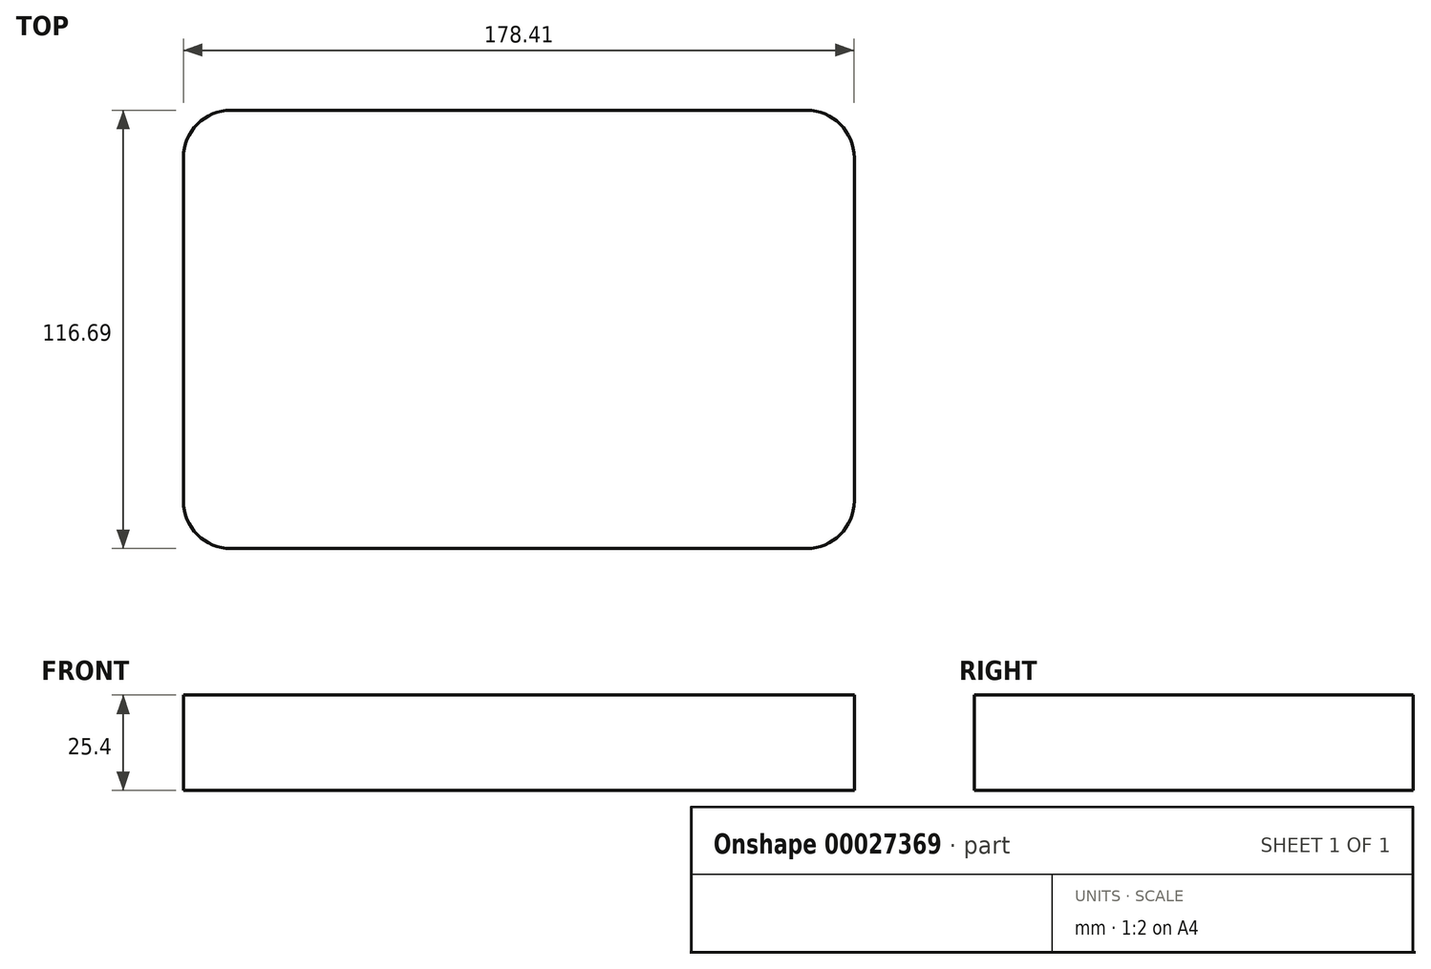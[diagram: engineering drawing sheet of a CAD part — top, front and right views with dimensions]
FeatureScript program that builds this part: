
annotation { "Feature Type Name" : "Feature", "Feature Type Description" : "" }
export const myFeature = defineFeature(function(context is Context, id is Id, definition is map)
    precondition{}
    {
        {
            var Q0;
            Q0=qCreatedBy(makeId("Top.planeOp"),FACE);
            var sketch = newSketch(context, id + "F0", { "sketchPlane" : qUnion([Q0])});
            skLineSegment(sketch, "E0.bottom", {"start": v(-115.93, 47.8) * mm, "end": v(37.08, 47.8) * mm});
            skLineSegment(sketch, "E0.top", {"start": v(-115.93, -68.9) * mm, "end": v(37.08, -68.9) * mm});
            skLineSegment(sketch, "E0.left", {"start": v(-128.63, 35.1) * mm, "end": v(-128.63, -56.2) * mm});
            skLineSegment(sketch, "E0.right", {"start": v(49.78, 35.1) * mm, "end": v(49.78, -56.2) * mm});
            skPoint(sketch, "E1.visualSharp", {"position": v(-128.63, 47.8) * mm});
            skArc(sketch, "E1.filletArc", {"start": v(-115.93, 47.8) * mm, "mid": v(-124.91, 44.08) * mm, "end": v(-128.63, 35.1) * mm});
            skPoint(sketch, "E2.visualSharp", {"position": v(49.78, 47.8) * mm});
            skArc(sketch, "E2.filletArc", {"start": v(49.78, 35.1) * mm, "mid": v(46.06, 44.08) * mm, "end": v(37.08, 47.8) * mm});
            skPoint(sketch, "E3.visualSharp", {"position": v(49.78, -68.9) * mm});
            skArc(sketch, "E3.filletArc", {"start": v(37.08, -68.9) * mm, "mid": v(46.06, -65.18) * mm, "end": v(49.78, -56.2) * mm});
            skPoint(sketch, "E4.visualSharp", {"position": v(-128.63, -68.9) * mm});
            skArc(sketch, "E4.filletArc", {"start": v(-128.63, -56.2) * mm, "mid": v(-124.91, -65.18) * mm, "end": v(-115.93, -68.9) * mm});
            skSolve(sketch);
        }
        {
            var Q0;
            Q0 = qSketchRegion(id + "F0", true);
            extrude(context, id + "F1", {"entities" : qUnion([Q0]), "depth" : 25.4 * mm});
        }
    });
